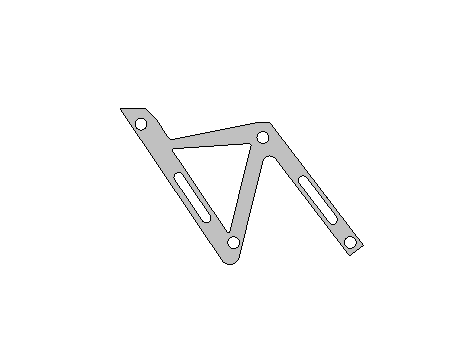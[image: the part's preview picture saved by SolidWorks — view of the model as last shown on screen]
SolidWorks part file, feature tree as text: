
SOLIDWORKS PART (.sldprt)
format: sldprt  version: not decoded by parser v0  size: 409,600 bytes
history: native  units: mm
features: extrude x37, sketch x1 (+10 scaffold rows collapsed)
feature tree (48):
  scaffold x10  (default folders/planes/origin — collapsed)
  sketch  "Sketch1"  dims[c1.D4=~5.100466mm c1.D10=10.16mm c1.D15=6.35mm c1.D17=5.08mm c1.D18=5.08mm c1.D2=2.54mm c1.D19=8.255mm c2.D10=3.81mm c2.D15=3.81mm c2.D1=12.7mm c2.D2=12.7mm c2.D3=~92.622632mm c3.D3=45.0deg c3.D4=101.6mm c3.D5=12.7mm c3.D6=12.7mm c3.D7=6.35mm c3.D8=76.2mm c3.D9=91.44mm c3.D10=6.35mm c3.D11=88.9mm c3.D12=120.65mm c3.D13=20.32mm c4.D10=~104.652849mm c5.D10=~3.185914deg c6.D10=~104.652849mm c7.D10=360.0deg c7.D14=6.35mm c7.D16=6.35mm c7.D20=15.24mm c7.D21=12.7mm c7.D22=7.62mm c7.D23=7.62mm c8.D16=7.62mm c8.D18=8.128mm c8.D24=3.556mm c8.D25=5.08mm]
  extrude  "Extrude2"  Depth=6.35mm cosMaterialEX=69000000000.0
  extrude  "sMaterialName"  [1 undecoded]
  extrude  "cosFMVItemName"  [1 undecoded]
  extrude  "cosMaterialName"  [1 undecoded]
  extrude  "cosComponentName"  [1 undecoded]
  extrude  "cosMaterialType"  [1 undecoded]
  extrude  "cosMaterialLibFile"  [1 undecoded]
  extrude  "cosMaterialRefPlaneName"  [1 undecoded]
  extrude  "sMaterialSourceName"  [1 undecoded]
  extrude  "sMaterialName"  [1 undecoded]
  extrude  "cosFMVItemName"  [1 undecoded]
  extrude  "cosMaterialName"  [1 undecoded]
  extrude  "cosComponentName"  [1 undecoded]
  extrude  "cosMaterialType"  [1 undecoded]
  extrude  "cosMaterialLibFile"  [1 undecoded]
  extrude  "cosMaterialRefPlaneName"  [1 undecoded]
  extrude  "cosRestraintRefPlaneName"  [1 undecoded]
  extrude  "cosFMVItemName"  [1 undecoded]
  extrude  "cosLBCSymbolColor"  Depth=0 cosRestraint7=0
  extrude  "cosRestraintRefPlaneName"  [1 undecoded]
  extrude  "cosFMVItemName"  [1 undecoded]
  extrude  "cosLBCSymbolColor"  [1 undecoded]
  extrude  "cosRestraintRefPlaneName"  [1 undecoded]
  extrude  "cosFMVItemName"  [1 undecoded]
  extrude  "cosLBCSymbolColor"  [1 undecoded]
  extrude  "cosForceRefPlaneName"  [1 undecoded]
  extrude  "cosFMVItemName"  [1 undecoded]
  extrude  "cosDistributionCoordSysName"  [1 undecoded]
  extrude  "cosLBCSymbolColor"  Depth=0 cosForce7=0
  extrude  "cosForceRefPlaneName"  [1 undecoded]
  extrude  "cosFMVItemName"  [1 undecoded]
  extrude  "cosDistributionCoordSysName"  [1 undecoded]
  extrude  "cosLBCSymbolColor"  [1 undecoded]
  extrude  "cosForceRefPlaneName"  [1 undecoded]
  extrude  "cosFMVItemName"  [1 undecoded]
  extrude  "cosDistributionCoordSysName"  [1 undecoded]
  extrude  "cosLBCSymbolColor"  Depth=0 cosFaceID=0
decode coverage: 5 of 38 modeling features carry decoded parameters
note: ~ marks probable driven/reference dimensions
note: 33 parameter values undecoded
summary: no parameter record found for 33 features
note: suppression state not decoded; provenance and decode notes live in map.json
